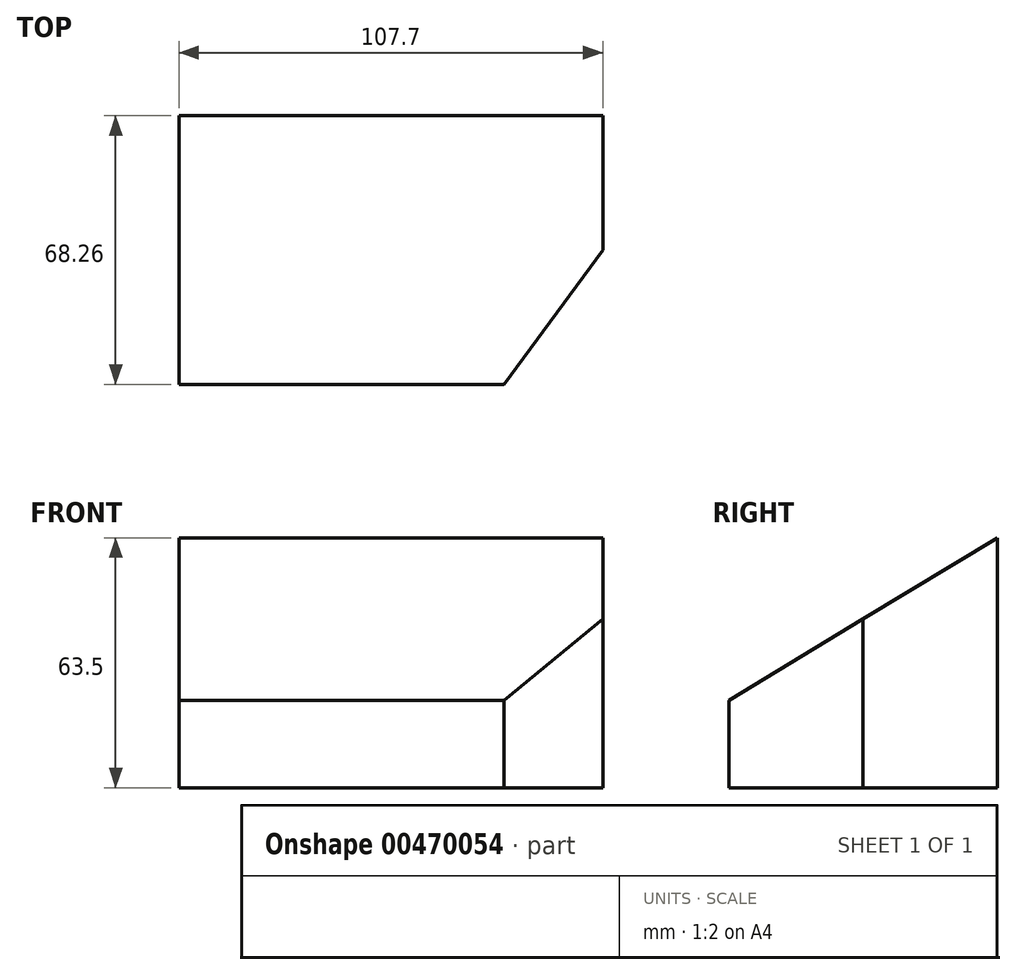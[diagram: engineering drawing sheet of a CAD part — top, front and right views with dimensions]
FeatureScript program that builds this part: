
annotation { "Feature Type Name" : "Feature", "Feature Type Description" : "" }
export const myFeature = defineFeature(function(context is Context, id is Id, definition is map)
    precondition{}
    {
        {
            var Q0;
            Q0=qCreatedBy(makeId("Top.planeOp"),FACE);
            var sketch = newSketch(context, id + "F0", { "sketchPlane" : qUnion([Q0])});
            skLineSegment(sketch, "E0.bottom", {"start": v(53.85, 34.13) * mm, "end": v(-53.85, 34.13) * mm});
            skLineSegment(sketch, "E0.top", {"start": v(28.82, -34.13) * mm, "end": v(-53.85, -34.13) * mm});
            skLineSegment(sketch, "E0.left", {"start": v(53.85, 34.13) * mm, "end": v(53.85, 0) * mm});
            skLineSegment(sketch, "E0.right", {"start": v(-53.85, 34.13) * mm, "end": v(-53.85, -34.13) * mm});
            skPoint(sketch, "E0.middle", {"position": v(0, 0) * mm});
            skLineSegment(sketch, "E1", {"start": v(53.85, 0) * mm, "end": v(28.82, -34.13) * mm});
            skPoint(sketch, "E2.orphan", {"position": v(53.85, -34.13) * mm});
            skSolve(sketch);
        }
        {
            var Q0;
            Q0=makeQuery(id+"F0.imprint","IMPRINT",FACE,{"disambiguationData":[TD([[makeQuery(id+"F0.imprint","IMPRINT",EDGE,{"derivedFrom":sQuery(id+"F0.wireOp",EDGE,"E0.bottom")}),1.0]])]});
            extrude(context, id + "F1", {"entities" : qUnion([Q0]), "depth" : 63.5 * mm});
        }
        {
            var Q0;
            Q0=makeQuery(id+"F1.opExtrude","SWEPT_FACE",FACE,{"disambiguationData":[OSD([sQuery(id+"F0.wireOp",EDGE,"E0.right")])]});
            var sketch = newSketch(context, id + "F2", { "sketchPlane" : qUnion([Q0])});
            skLineSegment(sketch, "E3", {"start": v(-34.13, 63.5) * mm, "end": v(34.13, 22.18) * mm});
            skLineSegment(sketch, "E4", {"start": v(34.13, 22.18) * mm, "end": v(34.13, 63.5) * mm});
            skLineSegment(sketch, "E5", {"start": v(34.13, 63.5) * mm, "end": v(-34.13, 63.5) * mm});
            skSolve(sketch);
        }
        {
            var Q0;
            Q0 = qSketchRegion(id + "F2", true);
            extrude(context, id + "F3", {"entities" : qUnion([Q0]), "operationType" : NewBodyOperationType.REMOVE, "endBound" : BoundingType.THROUGH_ALL, "oppositeDirection" : true, "depth" : 25.4 * mm});
        }
    });
